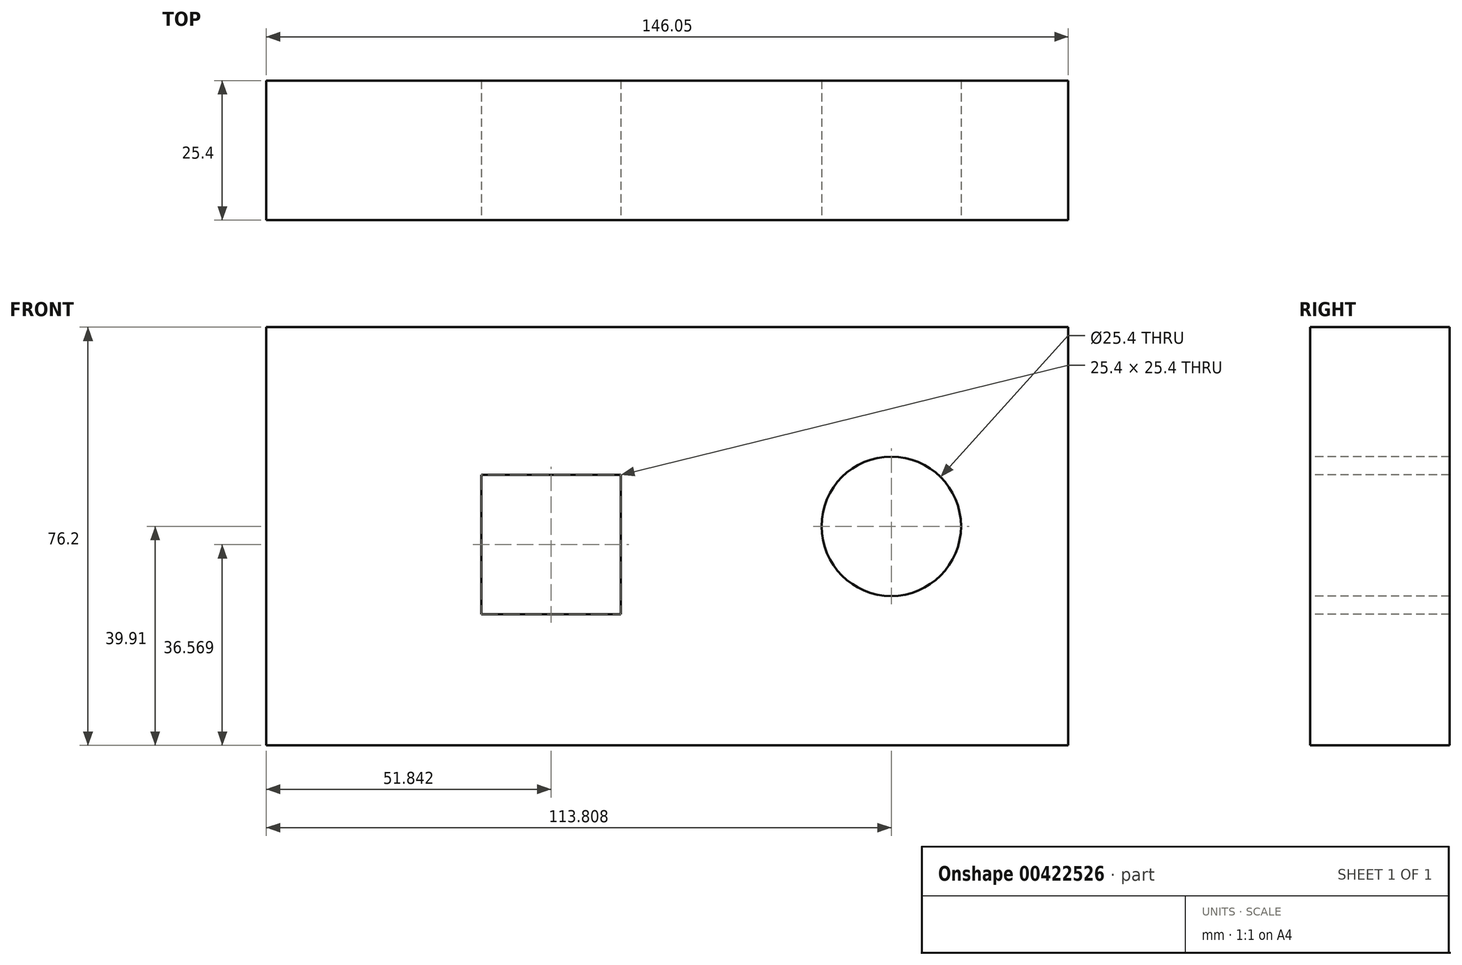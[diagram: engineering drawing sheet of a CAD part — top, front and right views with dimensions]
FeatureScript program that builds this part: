
annotation { "Feature Type Name" : "Feature", "Feature Type Description" : "" }
export const myFeature = defineFeature(function(context is Context, id is Id, definition is map)
    precondition{}
    {
        {
            var Q0;
            Q0=qCreatedBy(makeId("Front.planeOp"),FACE);
            var sketch = newSketch(context, id + "F0", { "sketchPlane" : qUnion([Q0])});
            skLineSegment(sketch, "E0", {"start": v(-76.2, 0) * mm, "end": v(69.86, 0) * mm});
            skLineSegment(sketch, "E1", {"start": v(69.86, 0) * mm, "end": v(69.86, 76.2) * mm});
            skLineSegment(sketch, "E2", {"start": v(69.86, 76.2) * mm, "end": v(-76.2, 76.2) * mm});
            skLineSegment(sketch, "E3", {"start": v(-76.2, 76.2) * mm, "end": v(-76.2, 0) * mm});
            skSolve(sketch);
        }
        {
            var Q0;
            Q0 = qSketchRegion(id + "F0", true);
            extrude(context, id + "F1", {"entities" : qUnion([Q0]), "depth" : 25.4 * mm});
        }
        {
            var Q0;
            Q0=makeQuery(id+"F1.opExtrude","CAP_FACE",FACE,{"disambiguationData":[OSD([sQuery(id+"F0.wireOp",EDGE,"E0"),sQuery(id+"F0.wireOp",EDGE,"E1"),sQuery(id+"F0.wireOp",EDGE,"E2"),sQuery(id+"F0.wireOp",EDGE,"E3")])],"isStart":false});
            var sketch = newSketch(context, id + "F2", { "sketchPlane" : qUnion([Q0])});
            skLineSegment(sketch, "E4.bottom", {"start": v(-37.05, 49.27) * mm, "end": v(-11.65, 49.27) * mm});
            skLineSegment(sketch, "E4.top", {"start": v(-37.05, 23.87) * mm, "end": v(-11.65, 23.87) * mm});
            skLineSegment(sketch, "E4.left", {"start": v(-37.05, 49.27) * mm, "end": v(-37.05, 23.87) * mm});
            skLineSegment(sketch, "E4.right", {"start": v(-11.65, 49.27) * mm, "end": v(-11.65, 23.87) * mm});
            skSolve(sketch);
        }
        {
            var Q0;
            Q0=makeQuery(id+"F2.imprint","IMPRINT",FACE,{"disambiguationData":[TD([[makeQuery(id+"F2.imprint","IMPRINT",EDGE,{"derivedFrom":sQuery(id+"F2.wireOp",EDGE,"E4.bottom")}),1.0]])]});
            var sketch = newSketch(context, id + "F3", { "sketchPlane" : qUnion([Q0])});
            skCircle(sketch, "E5", {"center": v(37.62, 39.9) * mm, "radius": 12.7 * mm});
            skSolve(sketch);
        }
        {
            var Q0;
            Q0 = qSketchRegion(id + "F3", true);
            extrude(context, id + "F4", {"entities" : qUnion([Q0]), "operationType" : NewBodyOperationType.REMOVE, "oppositeDirection" : true, "depth" : 2540 * mm});
        }
        {
            var Q0;
            Q0 = qSketchRegion(id + "F2", true);
            extrude(context, id + "F5", {"entities" : qUnion([Q0]), "operationType" : NewBodyOperationType.REMOVE, "oppositeDirection" : true, "depth" : 2540 * mm});
        }
    });
